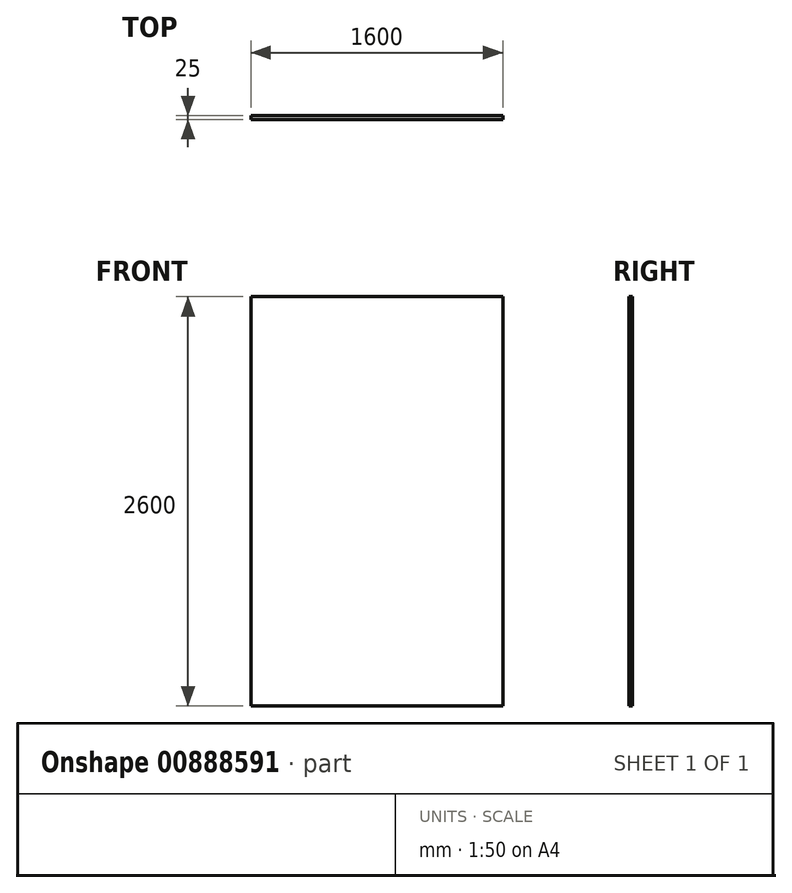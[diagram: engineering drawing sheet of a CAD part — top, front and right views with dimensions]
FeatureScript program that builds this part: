
annotation { "Feature Type Name" : "Feature", "Feature Type Description" : "" }
export const myFeature = defineFeature(function(context is Context, id is Id, definition is map)
    precondition{}
    {
        {
            var Q0;
            Q0=qCreatedBy(makeId("Front.planeOp"),FACE);
            var sketch = newSketch(context, id + "F0", { "sketchPlane" : qUnion([Q0])});
            skLineSegment(sketch, "E0.bottom", {"start": v(-1600, 2600) * mm, "end": v(0, 2600) * mm});
            skLineSegment(sketch, "E0.top", {"start": v(-1600, 0) * mm, "end": v(0, 0) * mm});
            skLineSegment(sketch, "E0.left", {"start": v(-1600, 2600) * mm, "end": v(-1600, 0) * mm});
            skLineSegment(sketch, "E0.right", {"start": v(0, 2600) * mm, "end": v(0, 0) * mm});
            skSolve(sketch);
        }
        {
            var Q0;
            Q0=makeQuery(id+"F0.imprint","IMPRINT",FACE,{"disambiguationData":[TD([[makeQuery(id+"F0.imprint","IMPRINT",EDGE,{"derivedFrom":sQuery(id+"F0.wireOp",EDGE,"E0.bottom")}),-1.0]])]});
            extrude(context, id + "F1", {"entities" : qUnion([Q0]), "depth" : 25 * mm, "offsetDistance" : 25 * mm});
        }
    });
